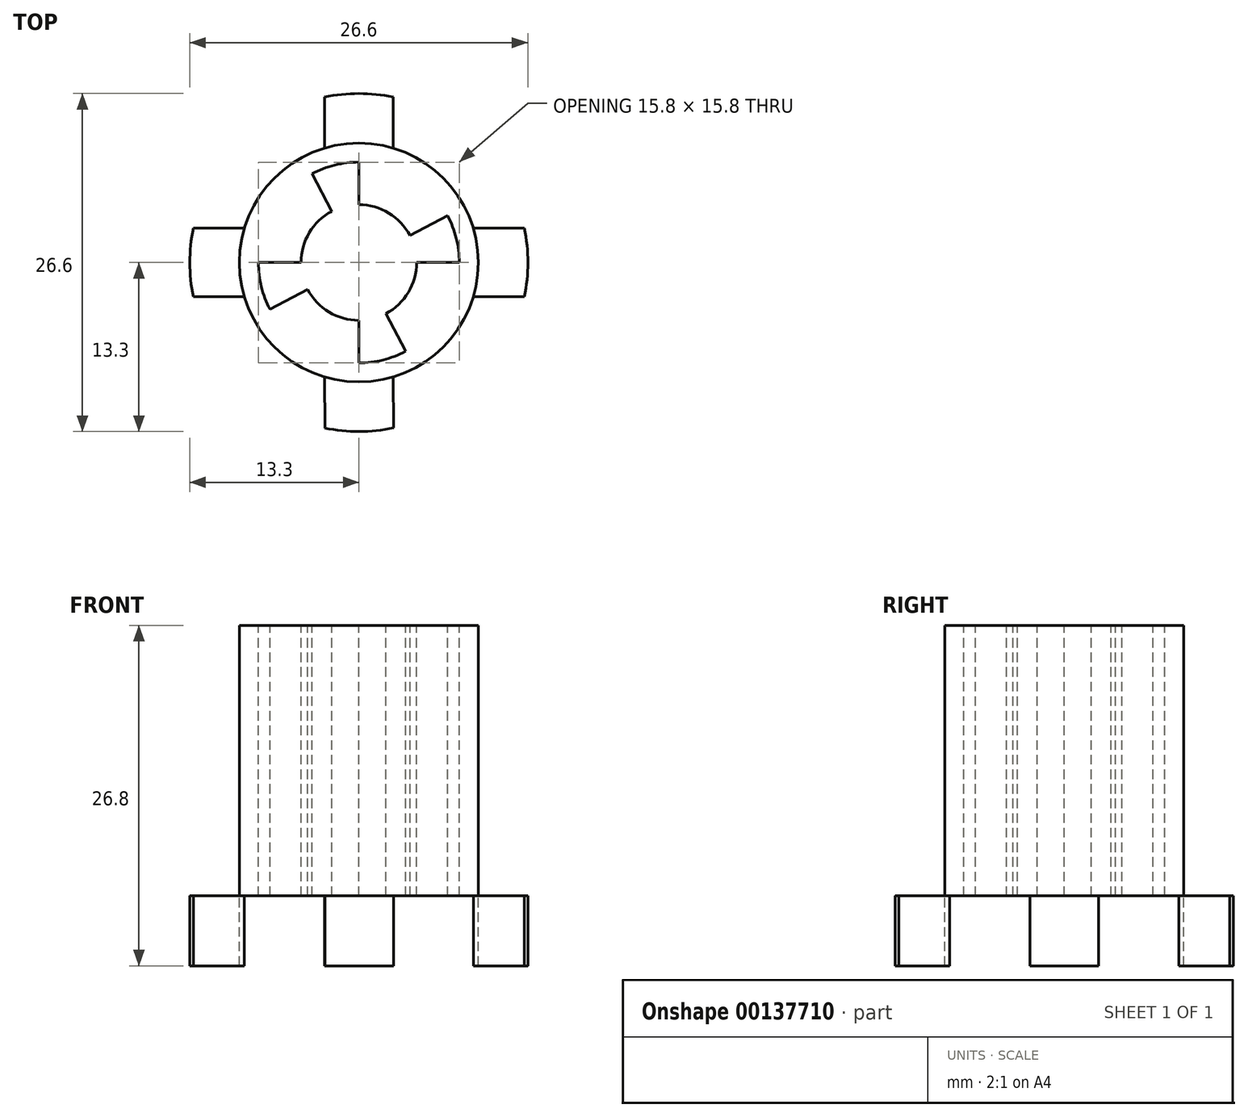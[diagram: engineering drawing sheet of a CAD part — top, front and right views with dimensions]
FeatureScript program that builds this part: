
annotation { "Feature Type Name" : "Feature", "Feature Type Description" : "" }
export const myFeature = defineFeature(function(context is Context, id is Id, definition is map)
    precondition{}
    {
        {
            var Q0;
            Q0=qCreatedBy(makeId("Top.planeOp"),FACE);
            var sketch = newSketch(context, id + "F0", { "sketchPlane" : qUnion([Q0])});
            skCircle(sketch, "E0", {"center": v(0, 0) * mm, "radius": 9.4 * mm});
            skCircle(sketch, "E1", {"center": v(0, 0) * mm, "radius": 13.3 * mm});
            skSolve(sketch);
        }
        {
            var Q0;
            Q0=makeQuery(id+"F0.imprint","IMPRINT",FACE,{"disambiguationData":[TD([[makeQuery(id+"F0.imprint","IMPRINT",EDGE,{"derivedFrom":sQuery(id+"F0.wireOp",EDGE,"E0")}),-1.0]])]});
            extrude(context, id + "F1", {"entities" : qUnion([Q0]), "oppositeDirection" : true, "depth" : 5.5 * mm});
        }
        {
            var Q0;
            Q0=qCreatedBy(makeId("Top.planeOp"),FACE);
            var sketch = newSketch(context, id + "F2", { "sketchPlane" : qUnion([Q0])});
            skCircle(sketch, "E2.0", {"center": v(0, 0) * mm, "radius": 9.4 * mm});
            skSolve(sketch);
        }
        {
            var Q0;
            Q0=qSketchRegion(id+"F2",true);
            extrude(context, id + "F3", {"entities" : qUnion([Q0]), "depth" : 21.3 * mm});
        }
        {
            var Q0;
            Q0=qCreatedBy(makeId("Top.planeOp"),FACE);
            var sketch = newSketch(context, id + "F4", { "sketchPlane" : qUnion([Q0])});
            skCircle(sketch, "E3.0", {"center": v(0, 0) * mm, "radius": 7.9 * mm});
            skLineSegment(sketch, "E4", {"start": v(0, -4.55) * mm, "end": v(0, -7.9) * mm});
            skLineSegment(sketch, "E5", {"start": v(2.12, -4.02) * mm, "end": v(3.69, -6.99) * mm});
            skLineSegment(sketch, "E6", {"start": v(4.55, 0) * mm, "end": v(7.9, 0) * mm});
            skLineSegment(sketch, "E7", {"start": v(4.02, 2.12) * mm, "end": v(6.99, 3.69) * mm});
            skLineSegment(sketch, "E8", {"start": v(0, 4.55) * mm, "end": v(0, 7.9) * mm});
            skLineSegment(sketch, "E9", {"start": v(-2.12, 4.02) * mm, "end": v(-3.69, 6.99) * mm});
            skLineSegment(sketch, "E10", {"start": v(-4.02, -2.12) * mm, "end": v(-6.99, -3.69) * mm});
            skLineSegment(sketch, "E11", {"start": v(-4.55, 0) * mm, "end": v(-7.9, 0) * mm});
            skArc(sketch, "E12", {"start": v(2.12, -4.02) * mm, "mid": v(3.9, -2.35) * mm, "end": v(4.55, 0) * mm});
            skArc(sketch, "E13.trimOffspring", {"start": v(4.02, 2.12) * mm, "mid": v(2.35, 3.9) * mm, "end": v(0, 4.55) * mm});
            skArc(sketch, "E14.trimOffspring", {"start": v(-2.12, 4.02) * mm, "mid": v(-3.9, 2.35) * mm, "end": v(-4.55, 0) * mm});
            skPoint(sketch, "E15.trimOffspring.end.orphan", {"position": v(0, 7.9) * mm});
            skPoint(sketch, "E16.orphan", {"position": v(-3.69, 6.99) * mm});
            skArc(sketch, "E17.trimOffspring", {"start": v(-4.02, -2.12) * mm, "mid": v(-2.35, -3.9) * mm, "end": v(0, -4.55) * mm});
            skSolve(sketch);
        }
        {
            var Q0;
            Q0=makeQuery(id+"F3.opExtrude","CAP_FACE",FACE,{"disambiguationData":[OSD([sQuery(id+"F2.wireOp",EDGE,"E2.0")])],"isStart":false});
            var sketch = newSketch(context, id + "F5", { "sketchPlane" : qUnion([Q0])});
            skCircle(sketch, "E18.0", {"center": v(0, 0) * mm, "radius": 7.9 * mm});
            skLineSegment(sketch, "E18.1", {"start": v(-2.12, 4.02) * mm, "end": v(-3.69, 6.99) * mm});
            skArc(sketch, "E18.2", {"start": v(-2.12, 4.02) * mm, "mid": v(-3.9, 2.35) * mm, "end": v(-4.55, 0) * mm});
            skLineSegment(sketch, "E18.3", {"start": v(-4.55, 0) * mm, "end": v(-7.9, 0) * mm});
            skArc(sketch, "E18.4", {"start": v(-4.02, -2.12) * mm, "mid": v(-2.35, -3.9) * mm, "end": v(0, -4.55) * mm});
            skArc(sketch, "E18.5", {"start": v(2.12, -4.02) * mm, "mid": v(3.9, -2.35) * mm, "end": v(4.55, 0) * mm});
            skArc(sketch, "E18.6", {"start": v(4.02, 2.12) * mm, "mid": v(2.35, 3.9) * mm, "end": v(0, 4.55) * mm});
            skLineSegment(sketch, "E18.7", {"start": v(0, 4.55) * mm, "end": v(0, 7.9) * mm});
            skLineSegment(sketch, "E18.8", {"start": v(4.02, 2.12) * mm, "end": v(6.99, 3.69) * mm});
            skLineSegment(sketch, "E18.9", {"start": v(2.12, -4.02) * mm, "end": v(3.69, -6.99) * mm});
            skLineSegment(sketch, "E18.10", {"start": v(-4.02, -2.12) * mm, "end": v(-6.99, -3.69) * mm});
            skLineSegment(sketch, "E19.0", {"start": v(4.55, 0) * mm, "end": v(7.9, 0) * mm});
            skLineSegment(sketch, "E19.1", {"start": v(0, -4.55) * mm, "end": v(0, -7.9) * mm});
            skSolve(sketch);
        }
        {
            var Q0;
            {var subQ3=sQuery(id+"F5.wireOp",EDGE,"E18.1");Q0=makeQuery(id+"F5.imprint","IMPRINT",FACE,{"disambiguationData":[TD([[makeQuery(id+"F5.imprint","IMPRINT",EDGE,{"derivedFrom":subQ3}),-1.0]])]});}
            extrude(context, id + "F6", {"entities" : qUnion([Q0]), "operationType" : NewBodyOperationType.REMOVE, "oppositeDirection" : true, "depth" : 25 * mm});
        }
        {
            var Q0;
            Q0=qCreatedBy(makeId("Top.planeOp"),FACE);
            var sketch = newSketch(context, id + "F7", { "sketchPlane" : qUnion([Q0])});
            skCircle(sketch, "E20.0", {"center": v(0, 0) * mm, "radius": 9.4 * mm});
            skCircle(sketch, "E20.1", {"center": v(0, 0) * mm, "radius": 13.3 * mm});
            skCircle(sketch, "E20.2.0", {"center": v(0, 0) * mm, "radius": 13.3 * mm});
            skLineSegment(sketch, "E21", {"start": v(0, -23.46) * mm, "end": v(0, 21.54) * mm, "construction": true});
            skLineSegment(sketch, "E22", {"start": v(-30.75, 0) * mm, "end": v(35, 0) * mm, "construction": true});
            skLineSegment(sketch, "E23.left", {"start": v(2.7, -9) * mm, "end": v(2.73, -13.02) * mm});
            skLineSegment(sketch, "E23.right", {"start": v(-2.7, -9) * mm, "end": v(-2.67, -13.03) * mm});
            skPoint(sketch, "E23.middle", {"position": v(0, -10.1) * mm});
            skLineSegment(sketch, "E24.bottom", {"start": v(13.02, -2.7) * mm, "end": v(9, -2.7) * mm});
            skLineSegment(sketch, "E24.top", {"start": v(13.02, 2.7) * mm, "end": v(9, 2.7) * mm});
            skPoint(sketch, "E24.middle", {"position": v(11.01, 0) * mm});
            skLineSegment(sketch, "E25.left", {"start": v(-2.7, 13.02) * mm, "end": v(-2.7, 9) * mm});
            skLineSegment(sketch, "E25.right", {"start": v(2.7, 13.02) * mm, "end": v(2.7, 9) * mm});
            skPoint(sketch, "E25.middle", {"position": v(0, 10.6) * mm});
            skLineSegment(sketch, "E26.bottom", {"start": v(-13.02, -2.7) * mm, "end": v(-9, -2.7) * mm});
            skLineSegment(sketch, "E26.top", {"start": v(-13.02, 2.7) * mm, "end": v(-9, 2.7) * mm});
            skLineSegment(sketch, "E26.right", {"start": v(-9, -2.7) * mm, "end": v(-9, -2.7) * mm});
            skPoint(sketch, "E26.middle", {"position": v(-11.01, 0) * mm});
            skPoint(sketch, "E27.orphan", {"position": v(9, -2.7) * mm});
            skPoint(sketch, "E28.orphan", {"position": v(9, 2.7) * mm});
            skLineSegment(sketch, "E29.trimOffspring", {"start": v(-9, 2.7) * mm, "end": v(-9, 2.7) * mm});
            skSolve(sketch);
        }
        {
            var Q0;
            {var subQ0=sQuery(id+"F7.wireOp",EDGE,"E23.left");Q0=makeQuery(id+"F7.imprint","IMPRINT",FACE,{"disambiguationData":[TD([[makeQuery(id+"F7.imprint","IMPRINT",EDGE,{"derivedFrom":subQ0}),1.0]])]});}
            var Q1;
            {var subQ0=sQuery(id+"F7.wireOp",EDGE,"E24.top");Q1=makeQuery(id+"F7.imprint","IMPRINT",FACE,{"disambiguationData":[TD([[makeQuery(id+"F7.imprint","IMPRINT",EDGE,{"derivedFrom":subQ0}),-1.0]])]});}
            var Q2;
            {var subQ0=sQuery(id+"F7.wireOp",EDGE,"E25.left");Q2=makeQuery(id+"F7.imprint","IMPRINT",FACE,{"disambiguationData":[TD([[makeQuery(id+"F7.imprint","IMPRINT",EDGE,{"derivedFrom":subQ0}),-1.0]])]});}
            var Q3;
            {var subQ0=sQuery(id+"F7.wireOp",EDGE,"E23.right");Q3=makeQuery(id+"F7.imprint","IMPRINT",FACE,{"disambiguationData":[TD([[makeQuery(id+"F7.imprint","IMPRINT",EDGE,{"derivedFrom":subQ0}),-1.0]])]});}
            extrude(context, id + "F8", {"entities" : qUnion([Q0, Q1, Q2, Q3]), "operationType" : NewBodyOperationType.REMOVE, "oppositeDirection" : true, "depth" : 25 * mm});
        }
    });
